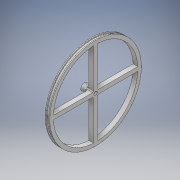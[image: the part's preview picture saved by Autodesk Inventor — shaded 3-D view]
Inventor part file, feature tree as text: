
AUTODESK INVENTOR PART (.ipt)
format: ipt  version: 2018 (Build 220112000, 112)  size: 209,920 bytes
history: native  units: mm
features: extrude x13, sketch x13, pattern_circular x1, fillet x1
ambient origin geometry x8: Origin, YZ Plane, XZ Plane, XY Plane, X Axis, Y Axis, Z Axis, Center Point
bodies: Solid1 (feature_tree)
feature tree (28):
  extrude  "Extrusion1"  Depth=3.5mm TaperAngle=0.0deg
  extrude  "Extrusion2"  Depth=1.0mm TaperAngle=0.0deg
  extrude  "Extrusion3"  Depth=1.0mm TaperAngle=0.0deg
  extrude  "Extrusion4"  Depth=6.0mm TaperAngle=0.0deg
  extrude  "Extrusion5"  Depth=10.0mm TaperAngle=0.0deg
  extrude  "Extrusion6"  Depth=1.0mm TaperAngle=0.0deg
  extrude  "Extrusion7"  Depth=1.0mm
  extrude  "Extrusion8"  Depth=4.0mm
  extrude  "Extrusion9"  Depth=40.0mm TaperAngle=360.0deg
  extrude  "Extrusion10"  Depth=2.0mm TaperAngle=0.0deg
  pattern_circular  "Circular Pattern1"  [2 undecoded]
  fillet  "Fillet1"  [1 undecoded]
  extrude  "Extrusion11"  [1 undecoded]
  extrude  "Extrusion12"  [1 undecoded]
  extrude  "Extrusion13"  [1 undecoded]
  sketch  "Sketch1"  dims[d0=88.0mm d1=3.5mm d2=0.0mm]
  sketch  "Sketch2"  dims[d3=90.0mm d4=1.0mm d5=0.0mm]
  sketch  "Sketch3"  dims[d6=90.0mm d7=1.0mm d8=0.0mm]
  sketch  "Sketch4"  dims[d9=83.0mm d10=6.0mm d11=0.0mm]
  sketch  "Sketch5"  dims[d12=7.0mm d13=10.0mm d14=0.0mm]
  sketch  "Sketch6"  dims[d15=2.0mm d16=0.0mm d17=1.0mm d18=0.0mm]
  sketch  "Sketch7"  dims[d19=1.0mm d20=0.0mm d21=3.25mm]
  sketch  "Sketch8"  dims[d22=10.0mm d23=0.0mm d24=4.0mm]
  sketch  "Sketch9"  dims[d25=4.5mm d26=0.0mm d27=40.0mm d28=360.0deg]
  sketch  "Sketch10"  dims[d30=2.0mm d31=2.0mm d32=0.0mm]
  sketch  "Sketch11"  dims[d33=4.0mm]
  sketch  "Sketch12"  dims[d34=3.3mm d35=0.0mm]
  sketch  "Sketch13"  dims[d36=3.3mm d37=0.0mm]
note: 6 required parameter values undecoded (feature->parameter linkage not recoverable at this tier; creation-order binding heuristic only, values carry confidence <= 0.55)
